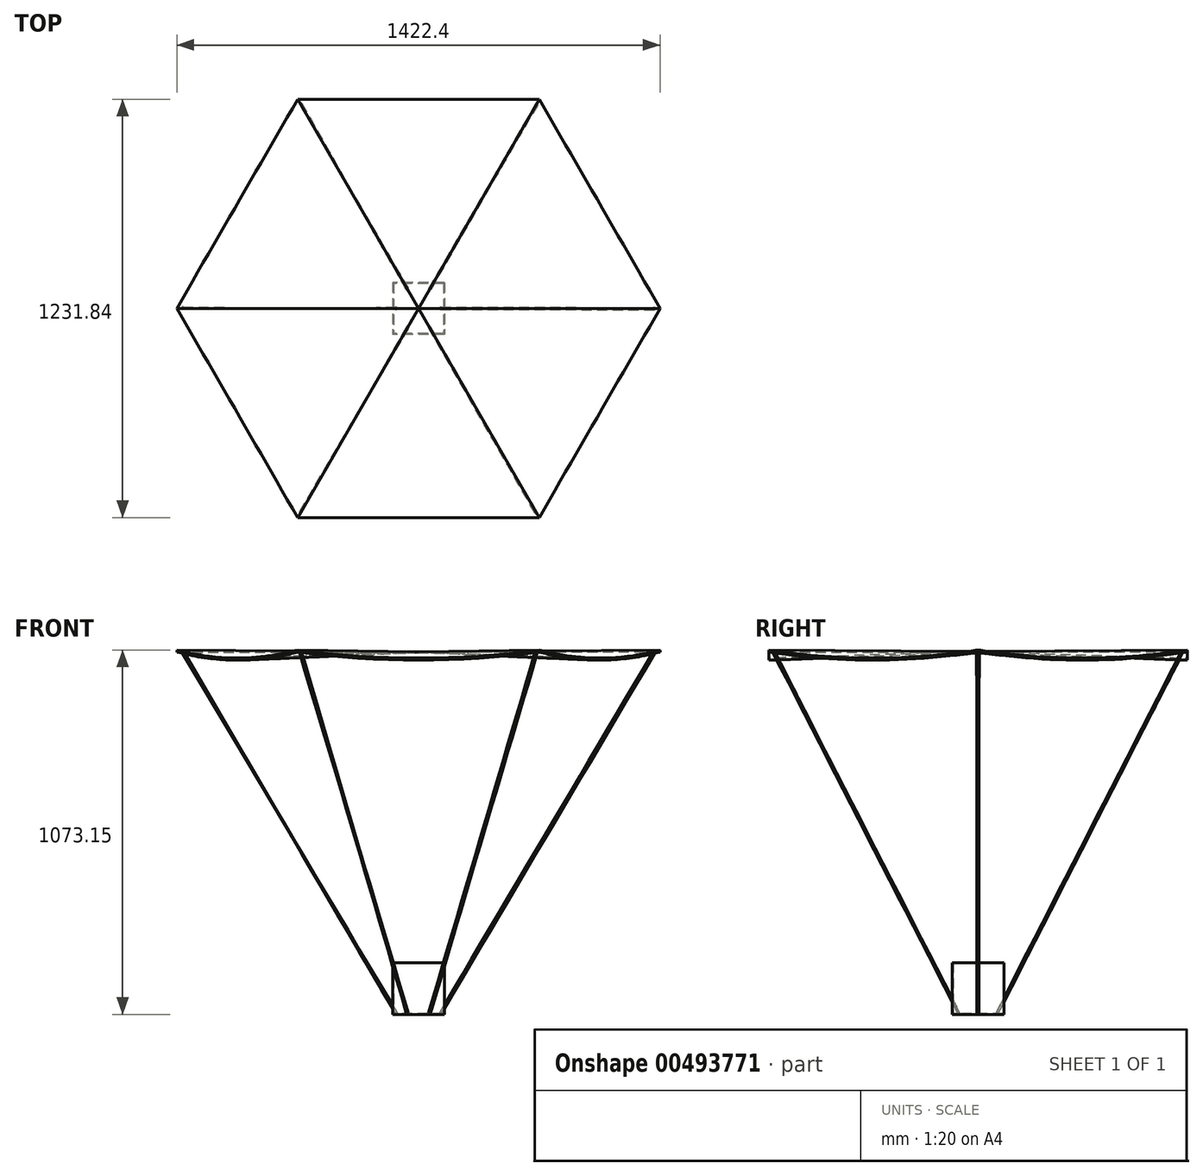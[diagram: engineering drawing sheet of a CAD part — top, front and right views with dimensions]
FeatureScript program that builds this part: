
annotation { "Feature Type Name" : "Feature", "Feature Type Description" : "" }
export const myFeature = defineFeature(function(context is Context, id is Id, definition is map)
    precondition{}
    {
        {
            var Q0;
            Q0=qCreatedBy(makeId("Top.planeOp"),FACE);
            var sketch = newSketch(context, id + "F0", { "sketchPlane" : qUnion([Q0])});
            skCircle(sketch, "E0.cCircle", {"center": v(0, 0) * mm, "radius": 615.92 * mm, "construction": true});
            skLineSegment(sketch, "E0.0", {"start": v(355.6, -615.92) * mm, "end": v(-355.6, -615.92) * mm});
            skLineSegment(sketch, "E0.1", {"start": v(-355.6, -615.92) * mm, "end": v(-711.2, 0) * mm});
            skLineSegment(sketch, "E0.2", {"start": v(-711.2, 0) * mm, "end": v(-355.6, 615.92) * mm});
            skLineSegment(sketch, "E0.3", {"start": v(-355.6, 615.92) * mm, "end": v(355.6, 615.92) * mm});
            skLineSegment(sketch, "E0.4", {"start": v(355.6, 615.92) * mm, "end": v(711.2, 0) * mm});
            skLineSegment(sketch, "E0.5", {"start": v(711.2, 0) * mm, "end": v(355.6, -615.92) * mm});
            skPoint(sketch, "E0.0.midPoint", {"position": v(0, -615.92) * mm});
            skLineSegment(sketch, "E1", {"start": v(0, 0) * mm, "end": v(355.6, -615.92) * mm});
            skLineSegment(sketch, "E2", {"start": v(0, 0) * mm, "end": v(711.2, 0) * mm});
            skLineSegment(sketch, "E3", {"start": v(0, 0) * mm, "end": v(355.6, 615.92) * mm});
            skLineSegment(sketch, "E4", {"start": v(0, 0) * mm, "end": v(-355.6, 615.92) * mm});
            skLineSegment(sketch, "E5", {"start": v(0, 0) * mm, "end": v(-711.2, 0) * mm});
            skLineSegment(sketch, "E6", {"start": v(0, 0) * mm, "end": v(-355.6, -615.92) * mm});
            skSolve(sketch);
        }
        {
            var Q0;
            Q0=qCreatedBy(makeId("Right.planeOp"),FACE);
            var Q1;
            Q1=sQuery(id+"F0.wireOp",EDGE,"E0.5");
            cPlane(context, id + "F1", {"entities" : qUnion([Q0, Q1]), "cplaneType" : CPlaneType.LINE_ANGLE, "offset" : 25.4 * mm, "angle" : 0 * degree, "width" : 152.4 * mm, "height" : 152.4 * mm});
        }
        {
            var Q0;
            Q0=qCreatedBy(makeId("Front.planeOp"),FACE);
            var Q1;
            Q1=sQuery(id+"F0.wireOp",EDGE,"E0.4");
            cPlane(context, id + "F2", {"entities" : qUnion([Q0, Q1]), "cplaneType" : CPlaneType.LINE_ANGLE, "offset" : 25.4 * mm, "angle" : 0 * degree, "width" : 152.4 * mm, "height" : 152.4 * mm});
        }
        {
            var Q0;
            Q0=qCreatedBy(makeId("Front.planeOp"),FACE);
            var Q1;
            Q1=sQuery(id+"F0.wireOp",EDGE,"E0.3");
            cPlane(context, id + "F3", {"entities" : qUnion([Q0, Q1]), "cplaneType" : CPlaneType.LINE_ANGLE, "offset" : 25.4 * mm, "angle" : 0 * degree, "width" : 152.4 * mm, "height" : 152.4 * mm});
        }
        {
            var Q0;
            Q0=qCreatedBy(makeId("Right.planeOp"),FACE);
            var Q1;
            Q1=sQuery(id+"F0.wireOp",EDGE,"E0.2");
            cPlane(context, id + "F4", {"entities" : qUnion([Q0, Q1]), "cplaneType" : CPlaneType.LINE_ANGLE, "offset" : 25.4 * mm, "angle" : 0 * degree, "width" : 152.4 * mm, "height" : 152.4 * mm});
        }
        {
            var Q0;
            Q0=qCreatedBy(id+"F1.planeOp",FACE);
            var sketch = newSketch(context, id + "F5", { "sketchPlane" : qUnion([Q0])});
            skArc(sketch, "E7", {"start": v(-355.6, 0) * mm, "mid": v(0, -23.81) * mm, "end": v(355.6, 0) * mm});
            skLineSegment(sketch, "E8", {"start": v(355.6, 0) * mm, "end": v(355.6, 6.35) * mm});
            skLineSegment(sketch, "E9", {"start": v(-355.6, 0) * mm, "end": v(-355.6, 6.35) * mm});
            skArc(sketch, "E10", {"start": v(-355.6, 6.35) * mm, "mid": v(0, -17.46) * mm, "end": v(355.6, 6.35) * mm});
            skSolve(sketch);
        }
        {
            var Q0;
            Q0=qCreatedBy(id+"F1.planeOp",FACE);
            cPlane(context, id + "F6", {"entities" : qUnion([Q0]), "cplaneType" : CPlaneType.OFFSET, "offset" : 615.92 * mm, "width" : 152.4 * mm, "height" : 152.4 * mm});
        }
        {
            var Q0;
            Q0=qCreatedBy(id+"F6.planeOp",FACE);
            var sketch = newSketch(context, id + "F7", { "sketchPlane" : qUnion([Q0])});
            skCircle(sketch, "E11", {"center": v(0, 0) * mm, "radius": 1.27 * mm});
            skSolve(sketch);
        }
        {
            var Q0;
            {var subQ0=sQuery(id+"F5.wireOp",EDGE,"E7");Q0=makeQuery(id+"F5.imprint","IMPRINT",FACE,{"disambiguationData":[TD([[makeQuery(id+"F5.imprint","IMPRINT",EDGE,{"derivedFrom":subQ0}),1.0]])]});}
            var Q1;
            Q1 = qSketchRegion(id + "F7", true);
            loft(context, id + "F8", {"sheetProfilesArray" : [{ "sheetProfileEntities" : qUnion([Q0]) }, { "sheetProfileEntities" : qUnion([Q1]) }]});
        }
        {
            var Q0;
            Q0=qCreatedBy(id+"F6.planeOp",FACE);
            var sketch = newSketch(context, id + "F9", { "sketchPlane" : qUnion([Q0])});
            skLineSegment(sketch, "E12", {"start": v(0, 0) * mm, "end": v(0, 36.34) * mm});
            skSolve(sketch);
        }
        {
            var Q0;
            {var subQ0=sQuery(id+"F5.wireOp",EDGE,"E7");Q0=makeQuery(id+"F8.opLoft","SWEPT_BODY",BODY,{"disambiguationData":[OSD([makeQuery(id+"F5.imprint","IMPRINT",FACE,{"disambiguationData":[TD([[makeQuery(id+"F5.imprint","IMPRINT",EDGE,{"derivedFrom":subQ0}),1.0]])]}),makeQuery(id+"F7.imprint","IMPRINT",FACE,{"disambiguationData":[TD([[makeQuery(id+"F7.imprint","IMPRINT",EDGE,{"derivedFrom":sQuery(id+"F7.wireOp",EDGE,"E11")}),1.0]])]})])]});}
            var Q1;
            Q1=sQuery(id+"F9.wireOp",EDGE,"E12");
            circularPattern(context, id + "F10", {"entities" : qUnion([Q0]), "axis" : qUnion([Q1]), "angle" : 360 * degree, "instanceCount" : 6, "equalSpace" : true});
        }
        {
            var Q0;
            Q0=qCreatedBy(makeId("Top.planeOp"),FACE);
            cPlane(context, id + "F11", {"entities" : qUnion([Q0]), "cplaneType" : CPlaneType.OFFSET, "offset" : 1066.8 * mm, "oppositeDirection" : true, "width" : 152.4 * mm, "height" : 152.4 * mm});
        }
        {
            var Q0;
            Q0=qCreatedBy(id+"F11.planeOp",FACE);
            var sketch = newSketch(context, id + "F12", { "sketchPlane" : qUnion([Q0])});
            skLineSegment(sketch, "E13.bottom", {"start": v(76.2, 76.2) * mm, "end": v(-76.2, 76.2) * mm});
            skLineSegment(sketch, "E13.top", {"start": v(76.2, -76.2) * mm, "end": v(-76.2, -76.2) * mm});
            skLineSegment(sketch, "E13.left", {"start": v(76.2, 76.2) * mm, "end": v(76.2, -76.2) * mm});
            skLineSegment(sketch, "E13.right", {"start": v(-76.2, 76.2) * mm, "end": v(-76.2, -76.2) * mm});
            skPoint(sketch, "E13.middle", {"position": v(0, 0) * mm});
            skSolve(sketch);
        }
        {
            var Q0;
            Q0=makeQuery(id+"F12.imprint","IMPRINT",FACE,{"disambiguationData":[TD([[makeQuery(id+"F12.imprint","IMPRINT",EDGE,{"derivedFrom":sQuery(id+"F12.wireOp",EDGE,"E13.bottom")}),1.0]])]});
            extrude(context, id + "F13", {"entities" : qUnion([Q0]), "depth" : 152.4 * mm});
        }
        {
            var Q0;
            Q0=makeQuery(id+"F13.opExtrude","CAP_FACE",FACE,{"disambiguationData":[OSD([sQuery(id+"F12.wireOp",EDGE,"E13.bottom"),sQuery(id+"F12.wireOp",EDGE,"E13.top"),sQuery(id+"F12.wireOp",EDGE,"E13.left"),sQuery(id+"F12.wireOp",EDGE,"E13.right")])],"isStart":false});
            shell(context, id + "F14", {"entities" : qUnion([Q0]), "thickness" : 2.54 * mm});
        }
        {
            var Q0;
            Q0=qCreatedBy(makeId("Top.planeOp"),FACE);
            var sketch = newSketch(context, id + "F15", { "sketchPlane" : qUnion([Q0])});
            skCircle(sketch, "E14", {"center": v(346.1, -601.22) * mm, "radius": 3.17 * mm});
            skCircle(sketch, "E15.1.0", {"center": v(693.72, -0.88) * mm, "radius": 3.17 * mm});
            skCircle(sketch, "E15.2.0", {"center": v(347.63, 600.34) * mm, "radius": 3.17 * mm});
            skCircle(sketch, "E15.3.0", {"center": v(-346.1, 601.22) * mm, "radius": 3.17 * mm});
            skCircle(sketch, "E15.4.0", {"center": v(-693.72, 0.88) * mm, "radius": 3.17 * mm});
            skCircle(sketch, "E15.5.0", {"center": v(-347.63, -600.34) * mm, "radius": 3.17 * mm});
            skPoint(sketch, "E15.center", {"position": v(0, 0) * mm});
            skSolve(sketch);
        }
        {
            var Q0;
            Q0 = qSketchRegion(id + "F15", true);
            extrude(context, id + "F16", {"entities" : qUnion([Q0]), "oppositeDirection" : true, "depth" : 0.5 * mm, "offsetDistance" : 25.4 * mm});
        }
        {
            var Q0;
            Q0=makeQuery(id+"F13.opExtrude","CAP_FACE",FACE,{"disambiguationData":[OSD([sQuery(id+"F12.wireOp",EDGE,"E13.bottom"),sQuery(id+"F12.wireOp",EDGE,"E13.top"),sQuery(id+"F12.wireOp",EDGE,"E13.left"),sQuery(id+"F12.wireOp",EDGE,"E13.right")])],"isStart":true});
            var sketch = newSketch(context, id + "F17", { "sketchPlane" : qUnion([Q0])});
            skCircle(sketch, "E16.cCircle", {"center": v(0, 0) * mm, "radius": 57.15 * mm, "construction": true});
            skLineSegment(sketch, "E16.0", {"start": v(-33, 57.15) * mm, "end": v(33, 57.15) * mm});
            skLineSegment(sketch, "E16.1", {"start": v(33, 57.15) * mm, "end": v(66, 0) * mm});
            skLineSegment(sketch, "E16.2", {"start": v(66, 0) * mm, "end": v(33, -57.15) * mm});
            skLineSegment(sketch, "E16.3", {"start": v(33, -57.15) * mm, "end": v(-33, -57.15) * mm});
            skLineSegment(sketch, "E16.4", {"start": v(-33, -57.15) * mm, "end": v(-66, 0) * mm});
            skLineSegment(sketch, "E16.5", {"start": v(-66, 0) * mm, "end": v(-33, 57.15) * mm});
            skPoint(sketch, "E16.0.midPoint", {"position": v(0, 57.15) * mm});
            skCircle(sketch, "E17", {"center": v(33, 57.15) * mm, "radius": 3.18 * mm});
            skSolve(sketch);
        }
        {
            var Q0;
            Q0=makeQuery(id+"F17.imprint","IMPRINT",FACE,{"disambiguationData":[TD([[makeQuery(id+"F17.imprint","IMPRINT",EDGE,{"derivedFrom":sQuery(id+"F17.wireOp",EDGE,"E16.0")}),1.0]])]});
            var sketch = newSketch(context, id + "F18", { "sketchPlane" : qUnion([Q0])});
            skCircle(sketch, "E18.cCircle", {"center": v(0, 0) * mm, "radius": 57.15 * mm, "construction": true});
            skLineSegment(sketch, "E18.0", {"start": v(-33, 57.15) * mm, "end": v(33, 57.15) * mm});
            skLineSegment(sketch, "E18.1", {"start": v(33, 57.15) * mm, "end": v(66, 0) * mm});
            skLineSegment(sketch, "E18.2", {"start": v(66, 0) * mm, "end": v(33, -57.15) * mm});
            skLineSegment(sketch, "E18.3", {"start": v(33, -57.15) * mm, "end": v(-33, -57.15) * mm});
            skLineSegment(sketch, "E18.4", {"start": v(-33, -57.15) * mm, "end": v(-66, 0) * mm});
            skLineSegment(sketch, "E18.5", {"start": v(-66, 0) * mm, "end": v(-33, 57.15) * mm});
            skPoint(sketch, "E18.0.midPoint", {"position": v(0, 57.15) * mm});
            skCircle(sketch, "E19", {"center": v(66, 0) * mm, "radius": 3.18 * mm});
            skSolve(sketch);
        }
        {
            var Q0;
            Q0=makeQuery(id+"F17.imprint","IMPRINT",FACE,{"disambiguationData":[TD([[makeQuery(id+"F17.imprint","IMPRINT",EDGE,{"derivedFrom":sQuery(id+"F17.wireOp",EDGE,"E16.0")}),1.0]])]});
            var sketch = newSketch(context, id + "F19", { "sketchPlane" : qUnion([Q0])});
            skCircle(sketch, "E20.cCircle", {"center": v(0, 0) * mm, "radius": 57.15 * mm, "construction": true});
            skLineSegment(sketch, "E20.0", {"start": v(-33, 57.15) * mm, "end": v(33, 57.15) * mm});
            skLineSegment(sketch, "E20.1", {"start": v(33, 57.15) * mm, "end": v(66, 0) * mm});
            skLineSegment(sketch, "E20.2", {"start": v(66, 0) * mm, "end": v(33, -57.15) * mm});
            skLineSegment(sketch, "E20.3", {"start": v(33, -57.15) * mm, "end": v(-33, -57.15) * mm});
            skLineSegment(sketch, "E20.4", {"start": v(-33, -57.15) * mm, "end": v(-66, 0) * mm});
            skLineSegment(sketch, "E20.5", {"start": v(-66, 0) * mm, "end": v(-33, 57.15) * mm});
            skPoint(sketch, "E20.0.midPoint", {"position": v(0, 57.15) * mm});
            skCircle(sketch, "E21", {"center": v(33, -57.15) * mm, "radius": 3.18 * mm});
            skSolve(sketch);
        }
        {
            var Q0;
            Q0=makeQuery(id+"F17.imprint","IMPRINT",FACE,{"disambiguationData":[TD([[makeQuery(id+"F17.imprint","IMPRINT",EDGE,{"derivedFrom":sQuery(id+"F17.wireOp",EDGE,"E16.0")}),1.0]])]});
            var sketch = newSketch(context, id + "F20", { "sketchPlane" : qUnion([Q0])});
            skCircle(sketch, "E22.cCircle", {"center": v(0, 0) * mm, "radius": 57.15 * mm, "construction": true});
            skLineSegment(sketch, "E22.0", {"start": v(-33, 57.15) * mm, "end": v(33, 57.15) * mm});
            skLineSegment(sketch, "E22.1", {"start": v(33, 57.15) * mm, "end": v(66, 0) * mm});
            skLineSegment(sketch, "E22.2", {"start": v(66, 0) * mm, "end": v(33, -57.15) * mm});
            skLineSegment(sketch, "E22.3", {"start": v(33, -57.15) * mm, "end": v(-33, -57.15) * mm});
            skLineSegment(sketch, "E22.4", {"start": v(-33, -57.15) * mm, "end": v(-66, 0) * mm});
            skLineSegment(sketch, "E22.5", {"start": v(-66, 0) * mm, "end": v(-33, 57.15) * mm});
            skPoint(sketch, "E22.0.midPoint", {"position": v(0, 57.15) * mm});
            skCircle(sketch, "E23", {"center": v(-33, -57.15) * mm, "radius": 3.18 * mm});
            skSolve(sketch);
        }
        {
            var Q0;
            Q0=makeQuery(id+"F17.imprint","IMPRINT",FACE,{"disambiguationData":[TD([[makeQuery(id+"F17.imprint","IMPRINT",EDGE,{"derivedFrom":sQuery(id+"F17.wireOp",EDGE,"E16.0")}),1.0]])]});
            var sketch = newSketch(context, id + "F21", { "sketchPlane" : qUnion([Q0])});
            skCircle(sketch, "E24.cCircle", {"center": v(0, 0) * mm, "radius": 57.15 * mm, "construction": true});
            skLineSegment(sketch, "E24.0", {"start": v(-33, 57.15) * mm, "end": v(33, 57.15) * mm});
            skLineSegment(sketch, "E24.1", {"start": v(33, 57.15) * mm, "end": v(66, 0) * mm});
            skLineSegment(sketch, "E24.2", {"start": v(66, 0) * mm, "end": v(33, -57.15) * mm});
            skLineSegment(sketch, "E24.3", {"start": v(33, -57.15) * mm, "end": v(-33, -57.15) * mm});
            skLineSegment(sketch, "E24.4", {"start": v(-33, -57.15) * mm, "end": v(-66, 0) * mm});
            skLineSegment(sketch, "E24.5", {"start": v(-66, 0) * mm, "end": v(-33, 57.15) * mm});
            skPoint(sketch, "E24.0.midPoint", {"position": v(0, 57.15) * mm});
            skCircle(sketch, "E25", {"center": v(-66, 0) * mm, "radius": 3.18 * mm});
            skSolve(sketch);
        }
        {
            var Q0;
            {var subQ6=sQuery(id+"F17.wireOp",EDGE,"E16.2");Q0=makeQuery(id+"F17.imprint","IMPRINT",FACE,{"disambiguationData":[TD([[makeQuery(id+"F17.imprint","IMPRINT",EDGE,{"derivedFrom":subQ6}),1.0]])]});}
            var sketch = newSketch(context, id + "F22", { "sketchPlane" : qUnion([Q0])});
            skCircle(sketch, "E26.cCircle", {"center": v(0, 0) * mm, "radius": 57.15 * mm, "construction": true});
            skLineSegment(sketch, "E26.0", {"start": v(-33, 57.15) * mm, "end": v(33, 57.15) * mm});
            skLineSegment(sketch, "E26.1", {"start": v(33, 57.15) * mm, "end": v(66, 0) * mm});
            skLineSegment(sketch, "E26.2", {"start": v(66, 0) * mm, "end": v(33, -57.15) * mm});
            skLineSegment(sketch, "E26.3", {"start": v(33, -57.15) * mm, "end": v(-33, -57.15) * mm});
            skLineSegment(sketch, "E26.4", {"start": v(-33, -57.15) * mm, "end": v(-66, 0) * mm});
            skLineSegment(sketch, "E26.5", {"start": v(-66, 0) * mm, "end": v(-33, 57.15) * mm});
            skPoint(sketch, "E26.0.midPoint", {"position": v(0, 57.15) * mm});
            skCircle(sketch, "E27", {"center": v(-33, 57.15) * mm, "radius": 3.18 * mm});
            skSolve(sketch);
        }
        {
            var Q0;
            {var subQ0=sQuery(id+"F17.wireOp",EDGE,"E16.1");var subQ1=sQuery(id+"F17.wireOp",EDGE,"E16.0");var subQ2=makeQuery(id+"F17.imprint","INTERSECT",VERTEX,{"derivedFrom":[subQ1,subQ0]});Q0=makeQuery(id+"F17.imprint","IMPRINT",FACE,{"disambiguationData":[TD([[makeQuery(id+"F17.imprint","IMPRINT",EDGE,{"disambiguationData":[TD([[subQ2,1.0]])],"derivedFrom":subQ1}),-1.0]])]});}
            var Q1;
            {var subQ0=sQuery(id+"F17.wireOp",EDGE,"E16.1");var subQ1=sQuery(id+"F17.wireOp",EDGE,"E16.0");var subQ2=makeQuery(id+"F17.imprint","INTERSECT",VERTEX,{"derivedFrom":[subQ1,subQ0]});Q1=makeQuery(id+"F17.imprint","IMPRINT",FACE,{"disambiguationData":[TD([[makeQuery(id+"F17.imprint","IMPRINT",EDGE,{"disambiguationData":[TD([[subQ2,1.0]])],"derivedFrom":subQ1}),1.0]])]});}
            extrude(context, id + "F23", {"entities" : qUnion([Q0, Q1]), "operationType" : NewBodyOperationType.ADD, "oppositeDirection" : true, "depth" : 5.08 * mm, "offsetDistance" : 25.4 * mm});
        }
        {
            var Q0;
            {var subQ0=sQuery(id+"F18.wireOp",EDGE,"E18.2");var subQ1=sQuery(id+"F18.wireOp",EDGE,"E18.1");var subQ2=makeQuery(id+"F18.imprint","INTERSECT",VERTEX,{"derivedFrom":[subQ1,subQ0]});Q0=makeQuery(id+"F18.imprint","IMPRINT",FACE,{"disambiguationData":[TD([[makeQuery(id+"F18.imprint","IMPRINT",EDGE,{"disambiguationData":[TD([[subQ2,1.0]])],"derivedFrom":subQ1}),1.0]])]});}
            var Q1;
            {var subQ0=sQuery(id+"F18.wireOp",EDGE,"E18.2");var subQ1=sQuery(id+"F18.wireOp",EDGE,"E18.1");var subQ2=makeQuery(id+"F18.imprint","INTERSECT",VERTEX,{"derivedFrom":[subQ1,subQ0]});Q1=makeQuery(id+"F18.imprint","IMPRINT",FACE,{"disambiguationData":[TD([[makeQuery(id+"F18.imprint","IMPRINT",EDGE,{"disambiguationData":[TD([[subQ2,1.0]])],"derivedFrom":subQ1}),-1.0]])]});}
            extrude(context, id + "F24", {"entities" : qUnion([Q0, Q1]), "operationType" : NewBodyOperationType.ADD, "oppositeDirection" : true, "depth" : 5.08 * mm, "offsetDistance" : 25.4 * mm});
        }
        {
            var Q0;
            {var subQ0=sQuery(id+"F19.wireOp",EDGE,"E20.3");var subQ1=sQuery(id+"F19.wireOp",EDGE,"E20.2");var subQ2=makeQuery(id+"F19.imprint","INTERSECT",VERTEX,{"derivedFrom":[subQ1,subQ0]});Q0=makeQuery(id+"F19.imprint","IMPRINT",FACE,{"disambiguationData":[TD([[makeQuery(id+"F19.imprint","IMPRINT",EDGE,{"disambiguationData":[TD([[subQ2,1.0]])],"derivedFrom":subQ1}),-1.0]])]});}
            var Q1;
            {var subQ0=sQuery(id+"F19.wireOp",EDGE,"E20.3");var subQ1=sQuery(id+"F19.wireOp",EDGE,"E20.2");var subQ2=makeQuery(id+"F19.imprint","INTERSECT",VERTEX,{"derivedFrom":[subQ1,subQ0]});Q1=makeQuery(id+"F19.imprint","IMPRINT",FACE,{"disambiguationData":[TD([[makeQuery(id+"F19.imprint","IMPRINT",EDGE,{"disambiguationData":[TD([[subQ2,1.0]])],"derivedFrom":subQ1}),1.0]])]});}
            extrude(context, id + "F25", {"entities" : qUnion([Q0, Q1]), "operationType" : NewBodyOperationType.ADD, "oppositeDirection" : true, "depth" : 5.08 * mm, "offsetDistance" : 25.4 * mm});
        }
        {
            var Q0;
            {var subQ0=sQuery(id+"F20.wireOp",EDGE,"E22.4");var subQ1=sQuery(id+"F20.wireOp",EDGE,"E22.3");var subQ2=makeQuery(id+"F20.imprint","INTERSECT",VERTEX,{"derivedFrom":[subQ1,subQ0]});Q0=makeQuery(id+"F20.imprint","IMPRINT",FACE,{"disambiguationData":[TD([[makeQuery(id+"F20.imprint","IMPRINT",EDGE,{"disambiguationData":[TD([[subQ2,1.0]])],"derivedFrom":subQ1}),-1.0]])]});}
            var Q1;
            {var subQ0=sQuery(id+"F20.wireOp",EDGE,"E22.4");var subQ1=sQuery(id+"F20.wireOp",EDGE,"E22.3");var subQ2=makeQuery(id+"F20.imprint","INTERSECT",VERTEX,{"derivedFrom":[subQ1,subQ0]});Q1=makeQuery(id+"F20.imprint","IMPRINT",FACE,{"disambiguationData":[TD([[makeQuery(id+"F20.imprint","IMPRINT",EDGE,{"disambiguationData":[TD([[subQ2,1.0]])],"derivedFrom":subQ1}),1.0]])]});}
            extrude(context, id + "F26", {"entities" : qUnion([Q0, Q1]), "operationType" : NewBodyOperationType.ADD, "oppositeDirection" : true, "depth" : 5.08 * mm, "offsetDistance" : 25.4 * mm});
        }
        {
            var Q0;
            {var subQ0=sQuery(id+"F21.wireOp",EDGE,"E24.5");var subQ1=sQuery(id+"F21.wireOp",EDGE,"E24.4");var subQ2=makeQuery(id+"F21.imprint","INTERSECT",VERTEX,{"derivedFrom":[subQ1,subQ0]});Q0=makeQuery(id+"F21.imprint","IMPRINT",FACE,{"disambiguationData":[TD([[makeQuery(id+"F21.imprint","IMPRINT",EDGE,{"disambiguationData":[TD([[subQ2,1.0]])],"derivedFrom":subQ1}),1.0]])]});}
            var Q1;
            {var subQ0=sQuery(id+"F21.wireOp",EDGE,"E24.5");var subQ1=sQuery(id+"F21.wireOp",EDGE,"E24.4");var subQ2=makeQuery(id+"F21.imprint","INTERSECT",VERTEX,{"derivedFrom":[subQ1,subQ0]});Q1=makeQuery(id+"F21.imprint","IMPRINT",FACE,{"disambiguationData":[TD([[makeQuery(id+"F21.imprint","IMPRINT",EDGE,{"disambiguationData":[TD([[subQ2,1.0]])],"derivedFrom":subQ1}),-1.0]])]});}
            extrude(context, id + "F27", {"entities" : qUnion([Q0, Q1]), "operationType" : NewBodyOperationType.ADD, "oppositeDirection" : true, "depth" : 5.08 * mm, "offsetDistance" : 25.4 * mm});
        }
        {
            var Q0;
            {var subQ0=sQuery(id+"F22.wireOp",EDGE,"E26.5");var subQ1=sQuery(id+"F22.wireOp",EDGE,"E26.0");var subQ2=makeQuery(id+"F22.imprint","INTERSECT",VERTEX,{"derivedFrom":[subQ1,subQ0]});Q0=makeQuery(id+"F22.imprint","IMPRINT",FACE,{"disambiguationData":[TD([[makeQuery(id+"F22.imprint","IMPRINT",EDGE,{"disambiguationData":[TD([[subQ2,-1.0]])],"derivedFrom":subQ1}),-1.0]])]});}
            var Q1;
            {var subQ0=sQuery(id+"F22.wireOp",EDGE,"E26.5");var subQ1=sQuery(id+"F22.wireOp",EDGE,"E26.0");var subQ2=makeQuery(id+"F22.imprint","INTERSECT",VERTEX,{"derivedFrom":[subQ1,subQ0]});Q1=makeQuery(id+"F22.imprint","IMPRINT",FACE,{"disambiguationData":[TD([[makeQuery(id+"F22.imprint","IMPRINT",EDGE,{"disambiguationData":[TD([[subQ2,-1.0]])],"derivedFrom":subQ1}),1.0]])]});}
            extrude(context, id + "F28", {"entities" : qUnion([Q0, Q1]), "operationType" : NewBodyOperationType.ADD, "oppositeDirection" : true, "depth" : 5.08 * mm, "offsetDistance" : 25.4 * mm});
        }
        {
            var Q0;
            Q0=makeQuery(id+"F16.opExtrude","CAP_FACE",FACE,{"disambiguationData":[OSD([sQuery(id+"F15.wireOp",EDGE,"E15.1.0")])],"isStart":false});
            var Q1;
            Q1=makeQuery(id+"F24.opExtrude","CAP_FACE",FACE,{"disambiguationData":[OSD([sQuery(id+"F18.wireOp",EDGE,"E19")])],"isStart":false});
            loft(context, id + "F29", {"sheetProfilesArray" : [{ "sheetProfileEntities" : qUnion([Q0]) }, { "sheetProfileEntities" : qUnion([Q1]) }]});
        }
        {
            var Q0;
            Q0=makeQuery(id+"F23.opExtrude","CAP_FACE",FACE,{"disambiguationData":[OSD([sQuery(id+"F17.wireOp",EDGE,"E17")])],"isStart":false});
            var Q1;
            Q1=makeQuery(id+"F16.opExtrude","CAP_FACE",FACE,{"disambiguationData":[OSD([sQuery(id+"F15.wireOp",EDGE,"E14")])],"isStart":false});
            loft(context, id + "F30", {"sheetProfilesArray" : [{ "sheetProfileEntities" : qUnion([Q0]) }, { "sheetProfileEntities" : qUnion([Q1]) }]});
        }
        {
            var Q0;
            Q0=makeQuery(id+"F16.opExtrude","CAP_FACE",FACE,{"disambiguationData":[OSD([sQuery(id+"F15.wireOp",EDGE,"E15.5.0")])],"isStart":false});
            var Q1;
            Q1=makeQuery(id+"F28.opExtrude","CAP_FACE",FACE,{"disambiguationData":[OSD([sQuery(id+"F22.wireOp",EDGE,"E27")])],"isStart":false});
            loft(context, id + "F31", {"sheetProfilesArray" : [{ "sheetProfileEntities" : qUnion([Q0]) }, { "sheetProfileEntities" : qUnion([Q1]) }]});
        }
        {
            var Q0;
            Q0=makeQuery(id+"F27.opExtrude","CAP_FACE",FACE,{"disambiguationData":[OSD([sQuery(id+"F21.wireOp",EDGE,"E25")])],"isStart":false});
            var Q1;
            Q1=makeQuery(id+"F16.opExtrude","CAP_FACE",FACE,{"disambiguationData":[OSD([sQuery(id+"F15.wireOp",EDGE,"E15.4.0")])],"isStart":false});
            loft(context, id + "F32", {"sheetProfilesArray" : [{ "sheetProfileEntities" : qUnion([Q0]) }, { "sheetProfileEntities" : qUnion([Q1]) }]});
        }
        {
            var Q0;
            Q0=makeQuery(id+"F26.opExtrude","CAP_FACE",FACE,{"disambiguationData":[OSD([sQuery(id+"F20.wireOp",EDGE,"E23")])],"isStart":false});
            var Q1;
            Q1=makeQuery(id+"F16.opExtrude","CAP_FACE",FACE,{"disambiguationData":[OSD([sQuery(id+"F15.wireOp",EDGE,"E15.3.0")])],"isStart":false});
            loft(context, id + "F33", {"sheetProfilesArray" : [{ "sheetProfileEntities" : qUnion([Q0]) }, { "sheetProfileEntities" : qUnion([Q1]) }]});
        }
        {
            var Q0;
            Q0=makeQuery(id+"F25.opExtrude","CAP_FACE",FACE,{"disambiguationData":[OSD([sQuery(id+"F19.wireOp",EDGE,"E21")])],"isStart":false});
            var Q1;
            Q1=makeQuery(id+"F16.opExtrude","CAP_FACE",FACE,{"disambiguationData":[OSD([sQuery(id+"F15.wireOp",EDGE,"E15.2.0")])],"isStart":false});
            loft(context, id + "F34", {"sheetProfilesArray" : [{ "sheetProfileEntities" : qUnion([Q0]) }, { "sheetProfileEntities" : qUnion([Q1]) }]});
        }
    });
